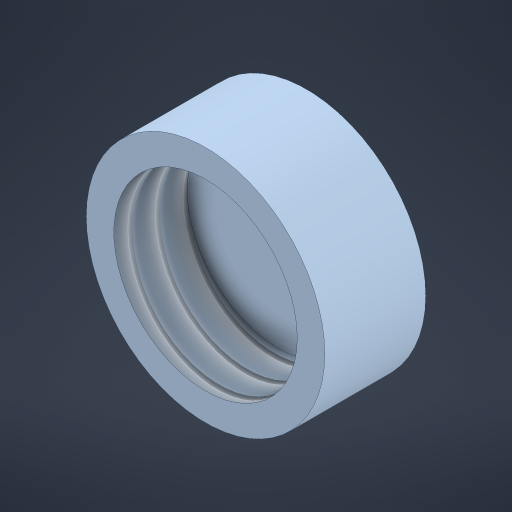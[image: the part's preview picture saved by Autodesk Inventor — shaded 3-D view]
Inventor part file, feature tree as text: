
AUTODESK INVENTOR PART (.ipt)
format: ipt  version: 2023 (Build 270158000, 158)  size: 215,552 bytes
history: native  units: mm
features: sketch x2, extrude x1, hole x1, thread x1
ambient origin geometry x8: Origin, YZ Plane, XZ Plane, XY Plane, X Axis, Y Axis, Z Axis, Center Point
bodies: Solid1 (feature_tree)
feature tree (5):
  extrude  "Extrusion1"  Depth=5.5mm TaperAngle=0.0deg
  hole  "Hole1"  [1 undecoded]
  thread  "Thread1"  [1 undecoded]
  sketch  "Sketch1"  dims[d0=13.0mm d1=5.5mm d2=0.0mm]
  sketch  "Sketch2"  dims[d3=10.0mm d4=6.0mm d5=4.0mm d6=2.0mm d7=90.0deg d8=4.0mm d9=0.0mm d10=4.0mm d11=0.0mm]
note: 2 required parameter values undecoded (feature->parameter linkage not recoverable at this tier; creation-order binding heuristic only, values carry confidence <= 0.55)
